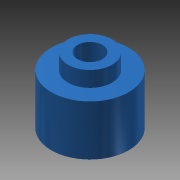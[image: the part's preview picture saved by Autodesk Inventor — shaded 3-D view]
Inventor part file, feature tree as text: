
AUTODESK INVENTOR PART (.ipt)
format: ipt  version: 2013 (Build 170138000, 138)  size: 88,576 bytes
history: native  units: mm
features: extrude x2, sketch x2
ambient origin geometry x8: Origin, YZ Plane, XZ Plane, XY Plane, X Axis, Y Axis, Z Axis, Center Point
bodies: Solid1 (feature_tree)
feature tree (4):
  extrude  "Extrusion1"  Depth=10.0mm
  extrude  "Extrusion2"  Depth=5.7mm
  sketch  "Sketch1"  dims[d0=3.2mm d1=10.0mm]
  sketch  "Sketch2"  dims[d2=6.5mm d3=0.0mm d4=5.7mm d5=2.0mm d6=0.0mm]
